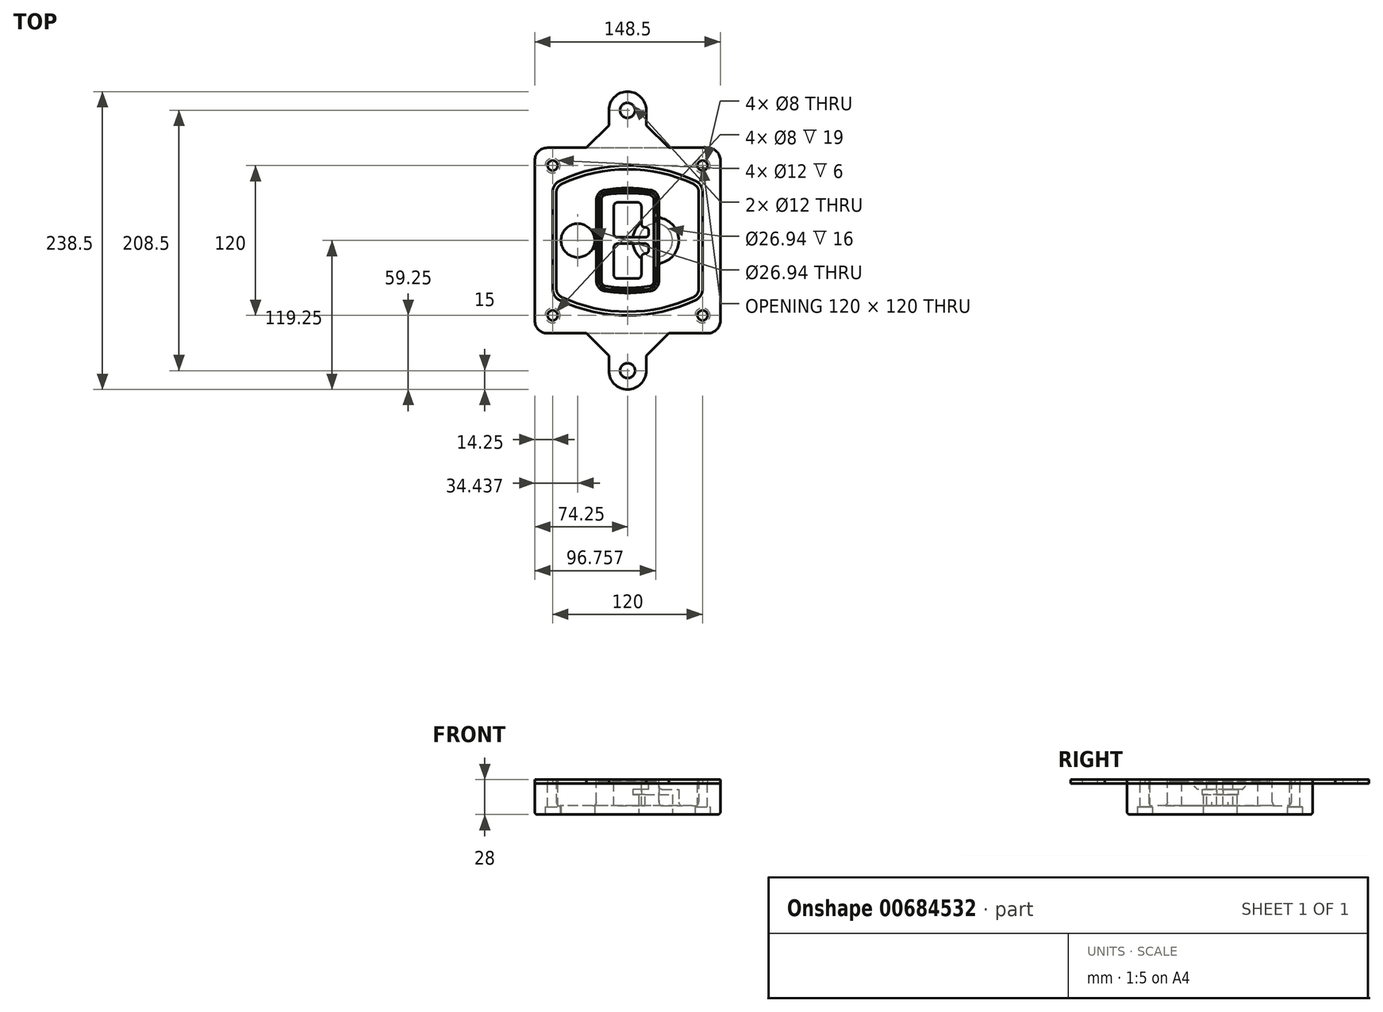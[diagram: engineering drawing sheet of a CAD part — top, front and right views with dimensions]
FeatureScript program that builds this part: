
annotation { "Feature Type Name" : "Feature", "Feature Type Description" : "" }
export const myFeature = defineFeature(function(context is Context, id is Id, definition is map)
    precondition{}
    {
        {
            var Q0;
            Q0=qCreatedBy(makeId("Top.planeOp"),FACE);
            var sketch = newSketch(context, id + "F0", { "sketchPlane" : qUnion([Q0])});
            skPoint(sketch, "E0.rect.middle", {"position": v(0, 0) * mm});
            skLineSegment(sketch, "E1.bottom", {"start": v(-64.25, -74.25) * mm, "end": v(64.25, -74.25) * mm});
            skLineSegment(sketch, "E1.top", {"start": v(-64.25, 74.25) * mm, "end": v(64.25, 74.25) * mm});
            skLineSegment(sketch, "E1.left", {"start": v(-74.25, -64.25) * mm, "end": v(-74.25, 64.25) * mm});
            skLineSegment(sketch, "E1.right", {"start": v(74.25, -64.25) * mm, "end": v(74.25, 64.25) * mm});
            skLineSegment(sketch, "E2", {"start": v(-74.25, 74.25) * mm, "end": v(74.25, -74.25) * mm, "construction": true});
            skLineSegment(sketch, "E3", {"start": v(74.25, 74.25) * mm, "end": v(-74.25, -74.25) * mm, "construction": true});
            skCircle(sketch, "E4", {"center": v(-60, 60) * mm, "radius": 4 * mm});
            skCircle(sketch, "E5", {"center": v(60, 60) * mm, "radius": 4 * mm});
            skCircle(sketch, "E6", {"center": v(60, -60) * mm, "radius": 4 * mm});
            skCircle(sketch, "E7", {"center": v(-60, -60) * mm, "radius": 4 * mm});
            skLineSegment(sketch, "E8", {"start": v(-60, 60) * mm, "end": v(60, 60) * mm, "construction": true});
            skLineSegment(sketch, "E9", {"start": v(60, 60) * mm, "end": v(60, -60) * mm, "construction": true});
            skLineSegment(sketch, "E10", {"start": v(60, -60) * mm, "end": v(-60, -60) * mm, "construction": true});
            skLineSegment(sketch, "E11", {"start": v(-60, -60) * mm, "end": v(-60, 60) * mm, "construction": true});
            skLineSegment(sketch, "E12", {"start": v(-60, 38.83) * mm, "end": v(-60, -38.83) * mm});
            skLineSegment(sketch, "E13", {"start": v(60, 38.83) * mm, "end": v(60, -38.83) * mm});
            skArc(sketch, "E14", {"start": v(54.26, 47.88) * mm, "mid": v(0, 60) * mm, "end": v(-54.26, 47.88) * mm});
            skArc(sketch, "E15", {"start": v(-54.26, -47.88) * mm, "mid": v(0, -60) * mm, "end": v(54.26, -47.88) * mm});
            skLineSegment(sketch, "E16", {"start": v(-60, 0) * mm, "end": v(60, 0) * mm, "construction": true});
            skPoint(sketch, "E17.visualSharp", {"position": v(-60, -45) * mm});
            skArc(sketch, "E17.filletArc", {"start": v(-60, -38.83) * mm, "mid": v(-58.44, -44.2) * mm, "end": v(-54.26, -47.88) * mm});
            skPoint(sketch, "E18.visualSharp", {"position": v(-60, 45) * mm});
            skArc(sketch, "E18.filletArc", {"start": v(-54.26, 47.88) * mm, "mid": v(-58.44, 44.2) * mm, "end": v(-60, 38.83) * mm});
            skPoint(sketch, "E19.visualSharp", {"position": v(60, 45) * mm});
            skArc(sketch, "E19.filletArc", {"start": v(60, 38.83) * mm, "mid": v(58.44, 44.2) * mm, "end": v(54.26, 47.88) * mm});
            skPoint(sketch, "E20.visualSharp", {"position": v(60, -45) * mm});
            skArc(sketch, "E20.filletArc", {"start": v(54.26, -47.88) * mm, "mid": v(58.44, -44.2) * mm, "end": v(60, -38.83) * mm});
            skPoint(sketch, "E21.visualSharp", {"position": v(-74.25, 74.25) * mm});
            skArc(sketch, "E21.filletArc", {"start": v(-64.25, 74.25) * mm, "mid": v(-71.32, 71.32) * mm, "end": v(-74.25, 64.25) * mm});
            skPoint(sketch, "E22.visualSharp", {"position": v(74.25, 74.25) * mm});
            skArc(sketch, "E22.filletArc", {"start": v(74.25, 64.25) * mm, "mid": v(71.32, 71.32) * mm, "end": v(64.25, 74.25) * mm});
            skPoint(sketch, "E23.visualSharp", {"position": v(74.25, -74.25) * mm});
            skArc(sketch, "E23.filletArc", {"start": v(64.25, -74.25) * mm, "mid": v(71.32, -71.32) * mm, "end": v(74.25, -64.25) * mm});
            skPoint(sketch, "E24.visualSharp", {"position": v(-74.25, -74.25) * mm});
            skArc(sketch, "E24.filletArc", {"start": v(-74.25, -64.25) * mm, "mid": v(-71.32, -71.32) * mm, "end": v(-64.25, -74.25) * mm});
            skArc(sketch, "E25.0", {"start": v(57, 38.83) * mm, "mid": v(55.9, 42.58) * mm, "end": v(52.98, 45.17) * mm});
            skLineSegment(sketch, "E25.1", {"start": v(57, 38.83) * mm, "end": v(57, -38.83) * mm});
            skArc(sketch, "E25.2", {"start": v(52.98, -45.17) * mm, "mid": v(55.9, -42.58) * mm, "end": v(57, -38.83) * mm});
            skArc(sketch, "E25.3", {"start": v(-52.98, -45.17) * mm, "mid": v(0, -57) * mm, "end": v(52.98, -45.17) * mm});
            skArc(sketch, "E25.4", {"start": v(-57, -38.83) * mm, "mid": v(-55.9, -42.58) * mm, "end": v(-52.98, -45.17) * mm});
            skArc(sketch, "E25.5", {"start": v(52.98, 45.17) * mm, "mid": v(0, 57) * mm, "end": v(-52.98, 45.17) * mm});
            skLineSegment(sketch, "E25.6", {"start": v(-57, 38.83) * mm, "end": v(-57, -38.83) * mm});
            skArc(sketch, "E25.7", {"start": v(-52.98, 45.17) * mm, "mid": v(-55.9, 42.58) * mm, "end": v(-57, 38.83) * mm});
            skArc(sketch, "E26.0", {"start": v(-55.96, 51.5) * mm, "mid": v(-61.82, 46.33) * mm, "end": v(-64, 38.83) * mm});
            skArc(sketch, "E26.1", {"start": v(55.96, 51.5) * mm, "mid": v(0, 64) * mm, "end": v(-55.96, 51.5) * mm});
            skArc(sketch, "E26.2", {"start": v(64, 38.83) * mm, "mid": v(61.82, 46.33) * mm, "end": v(55.96, 51.5) * mm});
            skLineSegment(sketch, "E26.3", {"start": v(64, 38.83) * mm, "end": v(64, -38.83) * mm});
            skArc(sketch, "E26.4", {"start": v(55.96, -51.5) * mm, "mid": v(61.82, -46.33) * mm, "end": v(64, -38.83) * mm});
            skLineSegment(sketch, "E26.5", {"start": v(-64, 38.83) * mm, "end": v(-64, -38.83) * mm});
            skArc(sketch, "E26.6", {"start": v(-55.96, -51.5) * mm, "mid": v(0, -64) * mm, "end": v(55.96, -51.5) * mm});
            skArc(sketch, "E26.7", {"start": v(-64, -38.83) * mm, "mid": v(-61.82, -46.33) * mm, "end": v(-55.96, -51.5) * mm});
            skLineSegment(sketch, "E27", {"start": v(0, 74.25) * mm, "end": v(0, 104.25) * mm, "construction": true});
            skCircle(sketch, "E28", {"center": v(0, 104.25) * mm, "radius": 6 * mm});
            skArc(sketch, "E29", {"start": v(-15, 104.25) * mm, "mid": v(0, 119.25) * mm, "end": v(15, 104.25) * mm});
            skLineSegment(sketch, "E30", {"start": v(-15, 104.25) * mm, "end": v(-15, 92.25) * mm});
            skLineSegment(sketch, "E31", {"start": v(15, 104.25) * mm, "end": v(15, 92.25) * mm});
            skLineSegment(sketch, "E32", {"start": v(-15, 92.25) * mm, "end": v(-33, 74.25) * mm});
            skLineSegment(sketch, "E33", {"start": v(15, 92.25) * mm, "end": v(33, 74.25) * mm});
            skLineSegment(sketch, "E34", {"start": v(0, -74.25) * mm, "end": v(0, -104.25) * mm, "construction": true});
            skCircle(sketch, "E35", {"center": v(0, -104.25) * mm, "radius": 6 * mm});
            skArc(sketch, "E36", {"start": v(15, -104.25) * mm, "mid": v(0, -119.25) * mm, "end": v(-15, -104.25) * mm});
            skLineSegment(sketch, "E37", {"start": v(15, -104.25) * mm, "end": v(15, -92.25) * mm});
            skLineSegment(sketch, "E38", {"start": v(-15, -104.25) * mm, "end": v(-15, -92.25) * mm});
            skLineSegment(sketch, "E39", {"start": v(15, -92.25) * mm, "end": v(33, -74.25) * mm});
            skLineSegment(sketch, "E40", {"start": v(-15, -92.25) * mm, "end": v(-33, -74.25) * mm});
            skSolve(sketch);
        }
        {
            var Q0;
            Q0=makeQuery(id+"F0.imprint","IMPRINT",FACE,{"disambiguationData":[TD([[makeQuery(id+"F0.imprint","IMPRINT",EDGE,{"derivedFrom":sQuery(id+"F0.wireOp",EDGE,"E1.bottom")}),1.0]])]});
            var Q1;
            Q1=makeQuery(id+"F0.imprint","IMPRINT",FACE,{"disambiguationData":[TD([[makeQuery(id+"F0.imprint","IMPRINT",EDGE,{"derivedFrom":sQuery(id+"F0.wireOp",EDGE,"E12")}),1.0]])]});
            var Q2;
            Q2=makeQuery(id+"F0.imprint","IMPRINT",FACE,{"disambiguationData":[TD([[makeQuery(id+"F0.imprint","IMPRINT",EDGE,{"derivedFrom":sQuery(id+"F0.wireOp",EDGE,"E25.0")}),1.0]])]});
            var Q3;
            Q3=makeQuery(id+"F0.imprint","IMPRINT",FACE,{"disambiguationData":[TD([[makeQuery(id+"F0.imprint","IMPRINT",EDGE,{"derivedFrom":sQuery(id+"F0.wireOp",EDGE,"E12")}),-1.0]])]});
            extrude(context, id + "F1", {"entities" : qUnion([Q0, Q1, Q2, Q3]), "oppositeDirection" : true, "depth" : 25 * mm});
        }
        {
            var Q0;
            Q0=makeQuery(id+"F0.imprint","IMPRINT",FACE,{"disambiguationData":[TD([[makeQuery(id+"F0.imprint","IMPRINT",EDGE,{"derivedFrom":sQuery(id+"F0.wireOp",EDGE,"E12")}),1.0]])]});
            extrude(context, id + "F2", {"entities" : qUnion([Q0]), "operationType" : NewBodyOperationType.ADD, "depth" : 3 * mm});
        }
        {
            var Q0;
            Q0=makeQuery(id+"F0.imprint","IMPRINT",FACE,{"disambiguationData":[TD([[makeQuery(id+"F0.imprint","IMPRINT",EDGE,{"derivedFrom":sQuery(id+"F0.wireOp",EDGE,"E25.0")}),1.0]])]});
            extrude(context, id + "F3", {"entities" : qUnion([Q0]), "operationType" : NewBodyOperationType.REMOVE, "oppositeDirection" : true, "depth" : 18 * mm});
        }
        {
            var Q0;
            Q0=makeQuery(id+"F2.opExtrude","CAP_FACE",FACE,{"disambiguationData":[OSD([sQuery(id+"F0.wireOp",EDGE,"E12"),sQuery(id+"F0.wireOp",EDGE,"E13"),sQuery(id+"F0.wireOp",EDGE,"E14"),sQuery(id+"F0.wireOp",EDGE,"E15"),sQuery(id+"F0.wireOp",EDGE,"E17.filletArc"),sQuery(id+"F0.wireOp",EDGE,"E18.filletArc"),sQuery(id+"F0.wireOp",EDGE,"E19.filletArc"),sQuery(id+"F0.wireOp",EDGE,"E20.filletArc"),sQuery(id+"F0.wireOp",EDGE,"E25.0"),sQuery(id+"F0.wireOp",EDGE,"E25.1"),sQuery(id+"F0.wireOp",EDGE,"E25.2"),sQuery(id+"F0.wireOp",EDGE,"E25.3"),sQuery(id+"F0.wireOp",EDGE,"E25.4"),sQuery(id+"F0.wireOp",EDGE,"E25.5"),sQuery(id+"F0.wireOp",EDGE,"E25.6"),sQuery(id+"F0.wireOp",EDGE,"E25.7")])],"isStart":false});
            var sketch = newSketch(context, id + "F4", { "sketchPlane" : qUnion([Q0])});
            skArc(sketch, "E41.0", {"start": v(-18.34, -40.45) * mm, "mid": v(0, -42) * mm, "end": v(18.34, -40.45) * mm});
            skArc(sketch, "E42.0", {"start": v(18.34, 40.45) * mm, "mid": v(0, 42) * mm, "end": v(-18.34, 40.45) * mm});
            skLineSegment(sketch, "E43", {"start": v(-25, 32.57) * mm, "end": v(-25, -32.57) * mm});
            skLineSegment(sketch, "E44", {"start": v(25, 32.57) * mm, "end": v(25, -32.57) * mm});
            skLineSegment(sketch, "E45", {"start": v(-25, 39.1) * mm, "end": v(25, 39.1) * mm, "construction": true});
            skLineSegment(sketch, "E46", {"start": v(-25, -39.1) * mm, "end": v(25, -39.1) * mm, "construction": true});
            skPoint(sketch, "E47.visualSharp", {"position": v(-25, 39.1) * mm});
            skArc(sketch, "E47.filletArc", {"start": v(-18.34, 40.45) * mm, "mid": v(-23.11, 37.73) * mm, "end": v(-25, 32.57) * mm});
            skPoint(sketch, "E48.visualSharp", {"position": v(25, 39.1) * mm});
            skArc(sketch, "E48.filletArc", {"start": v(25, 32.57) * mm, "mid": v(23.11, 37.73) * mm, "end": v(18.34, 40.45) * mm});
            skPoint(sketch, "E49.visualSharp", {"position": v(25, -39.1) * mm});
            skArc(sketch, "E49.filletArc", {"start": v(18.34, -40.45) * mm, "mid": v(23.11, -37.73) * mm, "end": v(25, -32.57) * mm});
            skPoint(sketch, "E50.visualSharp", {"position": v(-25, -39.1) * mm});
            skArc(sketch, "E50.filletArc", {"start": v(-25, -32.57) * mm, "mid": v(-23.11, -37.73) * mm, "end": v(-18.34, -40.45) * mm});
            skArc(sketch, "E51.0", {"start": v(52.98, 45.17) * mm, "mid": v(0, 57) * mm, "end": v(-52.98, 45.17) * mm});
            skArc(sketch, "E51.1", {"start": v(-52.98, 45.17) * mm, "mid": v(-55.9, 42.58) * mm, "end": v(-57, 38.83) * mm});
            skLineSegment(sketch, "E51.2", {"start": v(-57, 38.83) * mm, "end": v(-57, -38.83) * mm});
            skArc(sketch, "E51.3", {"start": v(-57, -38.83) * mm, "mid": v(-55.9, -42.58) * mm, "end": v(-52.98, -45.17) * mm});
            skArc(sketch, "E51.4", {"start": v(-52.98, -45.17) * mm, "mid": v(0, -57) * mm, "end": v(52.98, -45.17) * mm});
            skArc(sketch, "E51.5", {"start": v(52.98, -45.17) * mm, "mid": v(55.9, -42.58) * mm, "end": v(57, -38.83) * mm});
            skLineSegment(sketch, "E51.6", {"start": v(57, 38.83) * mm, "end": v(57, -38.83) * mm});
            skArc(sketch, "E51.7", {"start": v(57, 38.83) * mm, "mid": v(55.9, 42.58) * mm, "end": v(52.98, 45.17) * mm});
            skLineSegment(sketch, "E52.0", {"start": v(23, 32.57) * mm, "end": v(23, -32.57) * mm});
            skArc(sketch, "E52.1", {"start": v(18, -38.48) * mm, "mid": v(21.58, -36.44) * mm, "end": v(23, -32.57) * mm});
            skArc(sketch, "E52.2", {"start": v(-18, -38.48) * mm, "mid": v(0, -40) * mm, "end": v(18, -38.48) * mm});
            skArc(sketch, "E52.3", {"start": v(-23, -32.57) * mm, "mid": v(-21.58, -36.44) * mm, "end": v(-18, -38.48) * mm});
            skLineSegment(sketch, "E52.4", {"start": v(-23, 32.57) * mm, "end": v(-23, -32.57) * mm});
            skArc(sketch, "E52.5", {"start": v(23, 32.57) * mm, "mid": v(21.58, 36.44) * mm, "end": v(18, 38.48) * mm});
            skArc(sketch, "E52.6", {"start": v(-18, 38.48) * mm, "mid": v(-21.58, 36.44) * mm, "end": v(-23, 32.57) * mm});
            skArc(sketch, "E52.7", {"start": v(18, 38.48) * mm, "mid": v(0, 40) * mm, "end": v(-18, 38.48) * mm});
            skArc(sketch, "E53.0", {"start": v(21, 32.57) * mm, "mid": v(20.06, 35.15) * mm, "end": v(17.67, 36.5) * mm});
            skLineSegment(sketch, "E53.1", {"start": v(21, 32.57) * mm, "end": v(21, -32.57) * mm});
            skArc(sketch, "E53.2", {"start": v(17.67, -36.5) * mm, "mid": v(20.06, -35.15) * mm, "end": v(21, -32.57) * mm});
            skArc(sketch, "E53.3", {"start": v(-17.67, -36.5) * mm, "mid": v(0, -38) * mm, "end": v(17.67, -36.5) * mm});
            skArc(sketch, "E53.4", {"start": v(-21, -32.57) * mm, "mid": v(-20.06, -35.15) * mm, "end": v(-17.67, -36.5) * mm});
            skArc(sketch, "E53.5", {"start": v(17.67, 36.5) * mm, "mid": v(0, 38) * mm, "end": v(-17.67, 36.5) * mm});
            skLineSegment(sketch, "E53.6", {"start": v(-21, 32.57) * mm, "end": v(-21, -32.57) * mm});
            skArc(sketch, "E53.7", {"start": v(-17.67, 36.5) * mm, "mid": v(-20.06, 35.15) * mm, "end": v(-21, 32.57) * mm});
            skLineSegment(sketch, "E54", {"start": v(-25, 0) * mm, "end": v(25, 0) * mm, "construction": true});
            skLineSegment(sketch, "E55", {"start": v(-11, 5.5) * mm, "end": v(-11, 27.5) * mm});
            skLineSegment(sketch, "E56", {"start": v(-8, 30.5) * mm, "end": v(8, 30.5) * mm});
            skLineSegment(sketch, "E57", {"start": v(11, 27.5) * mm, "end": v(11, 13.5) * mm});
            skLineSegment(sketch, "E58", {"start": v(14, 10.5) * mm, "end": v(14, 10.5) * mm});
            skLineSegment(sketch, "E59", {"start": v(17, 7.5) * mm, "end": v(17, 5.5) * mm});
            skLineSegment(sketch, "E60", {"start": v(14, 2.5) * mm, "end": v(-8, 2.5) * mm});
            skPoint(sketch, "E61.visualSharp", {"position": v(-11, 30.5) * mm});
            skArc(sketch, "E61.filletArc", {"start": v(-8, 30.5) * mm, "mid": v(-10.12, 29.62) * mm, "end": v(-11, 27.5) * mm});
            skPoint(sketch, "E62.visualSharp", {"position": v(11, 30.5) * mm});
            skArc(sketch, "E62.filletArc", {"start": v(11, 27.5) * mm, "mid": v(10.12, 29.62) * mm, "end": v(8, 30.5) * mm});
            skPoint(sketch, "E63.visualSharp", {"position": v(11, 10.5) * mm});
            skArc(sketch, "E63.filletArc", {"start": v(11, 13.5) * mm, "mid": v(11.88, 11.38) * mm, "end": v(14, 10.5) * mm});
            skPoint(sketch, "E64.visualSharp", {"position": v(17, 10.5) * mm});
            skArc(sketch, "E64.filletArc", {"start": v(17, 7.5) * mm, "mid": v(16.12, 9.62) * mm, "end": v(14, 10.5) * mm});
            skPoint(sketch, "E65.visualSharp", {"position": v(17, 2.5) * mm});
            skArc(sketch, "E65.filletArc", {"start": v(14, 2.5) * mm, "mid": v(16.12, 3.38) * mm, "end": v(17, 5.5) * mm});
            skPoint(sketch, "E66.visualSharp", {"position": v(-11, 2.5) * mm});
            skArc(sketch, "E66.filletArc", {"start": v(-11, 5.5) * mm, "mid": v(-10.12, 3.38) * mm, "end": v(-8, 2.5) * mm});
            skLineSegment(sketch, "E67.0.MirrorCS", {"start": v(14, -2.5) * mm, "end": v(-8, -2.5) * mm});
            skArc(sketch, "E68.0.MirrorCS", {"start": v(-11, -5.5) * mm, "mid": v(-10.12, -3.38) * mm, "end": v(-8, -2.5) * mm});
            skLineSegment(sketch, "E69.0.MirrorCS", {"start": v(-11, -5.5) * mm, "end": v(-11, -27.5) * mm});
            skArc(sketch, "E70.0.MirrorCS", {"start": v(-8, -30.5) * mm, "mid": v(-10.12, -29.62) * mm, "end": v(-11, -27.5) * mm});
            skLineSegment(sketch, "E71.0.MirrorCS", {"start": v(-8, -30.5) * mm, "end": v(8, -30.5) * mm});
            skArc(sketch, "E72.0.MirrorCS", {"start": v(11, -27.5) * mm, "mid": v(10.12, -29.62) * mm, "end": v(8, -30.5) * mm});
            skLineSegment(sketch, "E73.0.MirrorCS", {"start": v(11, -27.5) * mm, "end": v(11, -13.5) * mm});
            skArc(sketch, "E74.0.MirrorCS", {"start": v(11, -13.5) * mm, "mid": v(11.88, -11.38) * mm, "end": v(14, -10.5) * mm});
            skArc(sketch, "E75.0.MirrorCS", {"start": v(17, -7.5) * mm, "mid": v(16.12, -9.62) * mm, "end": v(14, -10.5) * mm});
            skLineSegment(sketch, "E76.0.MirrorCS", {"start": v(17, -7.5) * mm, "end": v(17, -5.5) * mm});
            skArc(sketch, "E77.0.MirrorCS", {"start": v(14, -2.5) * mm, "mid": v(16.12, -3.38) * mm, "end": v(17, -5.5) * mm});
            skSolve(sketch);
        }
        {
            var Q0;
            Q0=makeQuery(id+"F4.imprint","IMPRINT",FACE,{"disambiguationData":[TD([[makeQuery(id+"F4.imprint","IMPRINT",EDGE,{"derivedFrom":sQuery(id+"F4.wireOp",EDGE,"E41.0")}),1.0]])]});
            var Q1;
            Q1=makeQuery(id+"F4.imprint","IMPRINT",FACE,{"disambiguationData":[TD([[makeQuery(id+"F4.imprint","IMPRINT",EDGE,{"derivedFrom":sQuery(id+"F4.wireOp",EDGE,"E52.0")}),-1.0]])]});
            var Q2;
            Q2=makeQuery(id+"F4.imprint","IMPRINT",FACE,{"disambiguationData":[TD([[makeQuery(id+"F4.imprint","IMPRINT",EDGE,{"derivedFrom":sQuery(id+"F4.wireOp",EDGE,"E53.0")}),1.0]])]});
            extrude(context, id + "F5", {"entities" : qUnion([Q0, Q1, Q2]), "operationType" : NewBodyOperationType.ADD, "endBound" : BoundingType.UP_TO_NEXT, "oppositeDirection" : true, "depth" : 25 * mm});
        }
        {
            var Q0;
            Q0=makeQuery(id+"F4.imprint","IMPRINT",FACE,{"disambiguationData":[TD([[makeQuery(id+"F4.imprint","IMPRINT",EDGE,{"derivedFrom":sQuery(id+"F4.wireOp",EDGE,"E52.0")}),-1.0]])]});
            extrude(context, id + "F6", {"entities" : qUnion([Q0]), "operationType" : NewBodyOperationType.REMOVE, "oppositeDirection" : true, "depth" : 2 * mm});
        }
        {
            var Q0;
            Q0=makeQuery(id+"F1.opExtrude","CAP_FACE",FACE,{"disambiguationData":[OSD([sQuery(id+"F0.wireOp",EDGE,"E1.bottom"),sQuery(id+"F0.wireOp",EDGE,"E1.top"),sQuery(id+"F0.wireOp",EDGE,"E1.left"),sQuery(id+"F0.wireOp",EDGE,"E1.right"),sQuery(id+"F0.wireOp",EDGE,"E4"),sQuery(id+"F0.wireOp",EDGE,"E5"),sQuery(id+"F0.wireOp",EDGE,"E6"),sQuery(id+"F0.wireOp",EDGE,"E7"),sQuery(id+"F0.wireOp",EDGE,"E21.filletArc"),sQuery(id+"F0.wireOp",EDGE,"E22.filletArc"),sQuery(id+"F0.wireOp",EDGE,"E23.filletArc"),sQuery(id+"F0.wireOp",EDGE,"E24.filletArc")])],"isStart":false});
            var sketch = newSketch(context, id + "F7", { "sketchPlane" : qUnion([Q0])});
            skCircle(sketch, "E78", {"center": v(22.5, 0) * mm, "radius": 13.47 * mm});
            skCircle(sketch, "E79", {"center": v(-39.81, 0) * mm, "radius": 13.47 * mm});
            skLineSegment(sketch, "E80", {"start": v(74.25, 0) * mm, "end": v(-74.25, 0) * mm});
            skCircle(sketch, "E81", {"center": v(22.5, 0) * mm, "radius": 18.47 * mm});
            skCircle(sketch, "E82", {"center": v(60, -60) * mm, "radius": 6 * mm});
            skCircle(sketch, "E83", {"center": v(-60, -60) * mm, "radius": 6 * mm});
            skCircle(sketch, "E84", {"center": v(-60, 60) * mm, "radius": 6 * mm});
            skCircle(sketch, "E85", {"center": v(60, 60) * mm, "radius": 6 * mm});
            skSolve(sketch);
        }
        {
            var Q0;
            {var subQ1=sQuery(id+"F7.wireOp",EDGE,"E80");var subQ4=sQuery(id+"F7.wireOp",EDGE,"E78");var subQ6=makeQuery(id+"F7.imprint","INTERSECT",VERTEX,{"disambiguationData":[OD(0.0)],"derivedFrom":[subQ4,subQ1]});Q0=makeQuery(id+"F7.imprint","IMPRINT",FACE,{"disambiguationData":[TD([[makeQuery(id+"F7.imprint","IMPRINT",EDGE,{"disambiguationData":[TD([[subQ6,-1.0]])],"derivedFrom":subQ4}),-1.0]])]});}
            var Q1;
            {var subQ0=sQuery(id+"F7.wireOp",EDGE,"E80");var subQ1=sQuery(id+"F7.wireOp",EDGE,"E78");var subQ3=makeQuery(id+"F7.imprint","INTERSECT",VERTEX,{"disambiguationData":[OD(0.0)],"derivedFrom":[subQ1,subQ0]});Q1=makeQuery(id+"F7.imprint","IMPRINT",FACE,{"disambiguationData":[TD([[makeQuery(id+"F7.imprint","IMPRINT",EDGE,{"disambiguationData":[TD([[subQ3,-1.0]])],"derivedFrom":subQ1}),1.0]])]});}
            var Q2;
            {var subQ0=sQuery(id+"F7.wireOp",EDGE,"E80");var subQ1=sQuery(id+"F7.wireOp",EDGE,"E78");var subQ3=makeQuery(id+"F7.imprint","INTERSECT",VERTEX,{"disambiguationData":[OD(0.0)],"derivedFrom":[subQ1,subQ0]});Q2=makeQuery(id+"F7.imprint","IMPRINT",FACE,{"disambiguationData":[TD([[makeQuery(id+"F7.imprint","IMPRINT",EDGE,{"disambiguationData":[TD([[subQ3,1.0]])],"derivedFrom":subQ1}),1.0]])]});}
            var Q3;
            {var subQ1=sQuery(id+"F7.wireOp",EDGE,"E80");var subQ4=sQuery(id+"F7.wireOp",EDGE,"E78");var subQ6=makeQuery(id+"F7.imprint","INTERSECT",VERTEX,{"disambiguationData":[OD(0.0)],"derivedFrom":[subQ4,subQ1]});Q3=makeQuery(id+"F7.imprint","IMPRINT",FACE,{"disambiguationData":[TD([[makeQuery(id+"F7.imprint","IMPRINT",EDGE,{"disambiguationData":[TD([[subQ6,1.0]])],"derivedFrom":subQ4}),-1.0]])]});}
            extrude(context, id + "F8", {"entities" : qUnion([Q0, Q1, Q2, Q3]), "operationType" : NewBodyOperationType.ADD, "oppositeDirection" : true, "depth" : 20 * mm});
        }
        {
            var Q0;
            {var subQ0=sQuery(id+"F7.wireOp",EDGE,"E80");var subQ1=sQuery(id+"F7.wireOp",EDGE,"E78");var subQ3=makeQuery(id+"F7.imprint","INTERSECT",VERTEX,{"disambiguationData":[OD(0.0)],"derivedFrom":[subQ1,subQ0]});Q0=makeQuery(id+"F7.imprint","IMPRINT",FACE,{"disambiguationData":[TD([[makeQuery(id+"F7.imprint","IMPRINT",EDGE,{"disambiguationData":[TD([[subQ3,-1.0]])],"derivedFrom":subQ1}),1.0]])]});}
            var Q1;
            {var subQ0=sQuery(id+"F7.wireOp",EDGE,"E80");var subQ1=sQuery(id+"F7.wireOp",EDGE,"E78");var subQ3=makeQuery(id+"F7.imprint","INTERSECT",VERTEX,{"disambiguationData":[OD(0.0)],"derivedFrom":[subQ1,subQ0]});Q1=makeQuery(id+"F7.imprint","IMPRINT",FACE,{"disambiguationData":[TD([[makeQuery(id+"F7.imprint","IMPRINT",EDGE,{"disambiguationData":[TD([[subQ3,1.0]])],"derivedFrom":subQ1}),1.0]])]});}
            extrude(context, id + "F9", {"entities" : qUnion([Q0, Q1]), "operationType" : NewBodyOperationType.REMOVE, "oppositeDirection" : true, "depth" : 16 * mm});
        }
        {
            var Q0;
            {var subQ0=sQuery(id+"F7.wireOp",EDGE,"E80");var subQ1=sQuery(id+"F7.wireOp",EDGE,"E79");var subQ3=makeQuery(id+"F7.imprint","INTERSECT",VERTEX,{"disambiguationData":[OD(0.0)],"derivedFrom":[subQ1,subQ0]});Q0=makeQuery(id+"F7.imprint","IMPRINT",FACE,{"disambiguationData":[TD([[makeQuery(id+"F7.imprint","IMPRINT",EDGE,{"disambiguationData":[TD([[subQ3,-1.0]])],"derivedFrom":subQ1}),1.0]])]});}
            var Q1;
            {var subQ0=sQuery(id+"F7.wireOp",EDGE,"E80");var subQ1=sQuery(id+"F7.wireOp",EDGE,"E79");var subQ3=makeQuery(id+"F7.imprint","INTERSECT",VERTEX,{"disambiguationData":[OD(0.0)],"derivedFrom":[subQ1,subQ0]});Q1=makeQuery(id+"F7.imprint","IMPRINT",FACE,{"disambiguationData":[TD([[makeQuery(id+"F7.imprint","IMPRINT",EDGE,{"disambiguationData":[TD([[subQ3,1.0]])],"derivedFrom":subQ1}),1.0]])]});}
            extrude(context, id + "F10", {"entities" : qUnion([Q0, Q1]), "operationType" : NewBodyOperationType.REMOVE, "oppositeDirection" : true, "depth" : 25 * mm});
        }
        {
            var Q0;
            Q0=makeQuery(id+"F7.imprint","IMPRINT",FACE,{"disambiguationData":[TD([[makeQuery(id+"F7.imprint","IMPRINT",EDGE,{"derivedFrom":sQuery(id+"F7.wireOp",EDGE,"E82")}),1.0]])]});
            var Q1;
            Q1=makeQuery(id+"F7.imprint","IMPRINT",FACE,{"disambiguationData":[TD([[makeQuery(id+"F7.imprint","IMPRINT",EDGE,{"derivedFrom":makeQuery(id+"F1.opExtrude","CAP_EDGE",EDGE,{"disambiguationData":[OSD([sQuery(id+"F0.wireOp",EDGE,"E5")])],"isStart":false})}),-1.0]])]});
            var Q2;
            Q2=makeQuery(id+"F7.imprint","IMPRINT",FACE,{"disambiguationData":[TD([[makeQuery(id+"F7.imprint","IMPRINT",EDGE,{"derivedFrom":sQuery(id+"F7.wireOp",EDGE,"E83")}),1.0]])]});
            var Q3;
            Q3=makeQuery(id+"F7.imprint","IMPRINT",FACE,{"disambiguationData":[TD([[makeQuery(id+"F7.imprint","IMPRINT",EDGE,{"derivedFrom":makeQuery(id+"F1.opExtrude","CAP_EDGE",EDGE,{"disambiguationData":[OSD([sQuery(id+"F0.wireOp",EDGE,"E4")])],"isStart":false})}),-1.0]])]});
            var Q4;
            Q4=makeQuery(id+"F7.imprint","IMPRINT",FACE,{"disambiguationData":[TD([[makeQuery(id+"F7.imprint","IMPRINT",EDGE,{"derivedFrom":sQuery(id+"F7.wireOp",EDGE,"E84")}),1.0]])]});
            var Q5;
            Q5=makeQuery(id+"F7.imprint","IMPRINT",FACE,{"disambiguationData":[TD([[makeQuery(id+"F7.imprint","IMPRINT",EDGE,{"derivedFrom":makeQuery(id+"F1.opExtrude","CAP_EDGE",EDGE,{"disambiguationData":[OSD([sQuery(id+"F0.wireOp",EDGE,"E7")])],"isStart":false})}),-1.0]])]});
            var Q6;
            Q6=makeQuery(id+"F7.imprint","IMPRINT",FACE,{"disambiguationData":[TD([[makeQuery(id+"F7.imprint","IMPRINT",EDGE,{"derivedFrom":sQuery(id+"F7.wireOp",EDGE,"E85")}),1.0]])]});
            var Q7;
            Q7=makeQuery(id+"F7.imprint","IMPRINT",FACE,{"disambiguationData":[TD([[makeQuery(id+"F7.imprint","IMPRINT",EDGE,{"derivedFrom":makeQuery(id+"F1.opExtrude","CAP_EDGE",EDGE,{"disambiguationData":[OSD([sQuery(id+"F0.wireOp",EDGE,"E6")])],"isStart":false})}),-1.0]])]});
            extrude(context, id + "F11", {"entities" : qUnion([Q0, Q1, Q2, Q3, Q4, Q5, Q6, Q7]), "operationType" : NewBodyOperationType.REMOVE, "oppositeDirection" : true, "depth" : 6 * mm});
        }
        {
            var Q0;
            Q0=makeQuery(id+"F9.boolean.opBoolean","COPY",FACE,{"derivedFrom":makeQuery(id+"F9.opExtrude","CAP_FACE",FACE,{"disambiguationData":[OSD([sQuery(id+"F7.wireOp",EDGE,"E78")])],"isStart":false})});
            var sketch = newSketch(context, id + "F12", { "sketchPlane" : qUnion([Q0])});
            skArc(sketch, "E86.0", {"start": v(11, 14.45) * mm, "mid": v(6.45, 9.13) * mm, "end": v(4.2, 2.5) * mm});
            skArc(sketch, "E86.1", {"start": v(4.2, -2.5) * mm, "mid": v(6.45, -9.13) * mm, "end": v(11, -14.45) * mm});
            skLineSegment(sketch, "E87", {"start": v(4.2, -2.5) * mm, "end": v(14, -2.5) * mm});
            skLineSegment(sketch, "E88.0", {"start": v(14, 2.5) * mm, "end": v(4.2, 2.5) * mm});
            skArc(sketch, "E88.1", {"start": v(14, 2.5) * mm, "mid": v(16.12, 3.38) * mm, "end": v(17, 5.5) * mm});
            skLineSegment(sketch, "E88.2", {"start": v(17, 7.5) * mm, "end": v(17, 5.5) * mm});
            skArc(sketch, "E88.3", {"start": v(17, 7.5) * mm, "mid": v(16.12, 9.62) * mm, "end": v(14, 10.5) * mm});
            skArc(sketch, "E88.4", {"start": v(11, 13.5) * mm, "mid": v(11.88, 11.38) * mm, "end": v(14, 10.5) * mm});
            skLineSegment(sketch, "E88.5", {"start": v(11, 14.45) * mm, "end": v(11, 13.5) * mm});
            skLineSegment(sketch, "E88.7", {"start": v(14, -2.5) * mm, "end": v(4.2, -2.5) * mm});
            skArc(sketch, "E88.8", {"start": v(14, -2.5) * mm, "mid": v(16.12, -3.38) * mm, "end": v(17, -5.5) * mm});
            skLineSegment(sketch, "E88.9", {"start": v(17, -7.5) * mm, "end": v(17, -5.5) * mm});
            skArc(sketch, "E88.10", {"start": v(17, -7.5) * mm, "mid": v(16.12, -9.62) * mm, "end": v(14, -10.5) * mm});
            skArc(sketch, "E88.11", {"start": v(11, -13.5) * mm, "mid": v(11.88, -11.38) * mm, "end": v(14, -10.5) * mm});
            skLineSegment(sketch, "E88.12", {"start": v(11, -14.45) * mm, "end": v(11, -13.5) * mm});
            skPoint(sketch, "E89.orphan", {"position": v(11, -27.5) * mm});
            skPoint(sketch, "E90.orphan", {"position": v(-8, -2.5) * mm});
            skPoint(sketch, "E91.orphan", {"position": v(-8, 2.5) * mm});
            skPoint(sketch, "E92.orphan", {"position": v(11, 27.5) * mm});
            skSolve(sketch);
        }
        {
            var Q0;
            {var subQ7=sQuery(id+"F12.wireOp",EDGE,"E86.0");var subQ14=sQuery(id+"F12.wireOp",EDGE,"E86.1");var subQ16=sQuery(id+"F12.wireOp",EDGE,"E88.1");var subQ18=sQuery(id+"F12.wireOp",EDGE,"E88.8");Q0=qUnion([makeQuery(id+"F12.imprint","IMPRINT",FACE,{"disambiguationData":[TD([[makeQuery(id+"F12.imprint","IMPRINT",EDGE,{"derivedFrom":subQ7}),1.0]])]}),makeQuery(id+"F12.imprint","IMPRINT",FACE,{"disambiguationData":[TD([[makeQuery(id+"F12.imprint","IMPRINT",EDGE,{"derivedFrom":subQ14}),1.0]])]}),makeQuery(id+"F12.imprint","IMPRINT",FACE,{"disambiguationData":[TD([[makeQuery(id+"F12.imprint","IMPRINT",EDGE,{"derivedFrom":subQ16}),1.0]])]}),makeQuery(id+"F12.imprint","IMPRINT",FACE,{"disambiguationData":[TD([[makeQuery(id+"F12.imprint","IMPRINT",EDGE,{"derivedFrom":subQ18}),-1.0]])]})]);}
            var Q1;
            Q1=makeQuery(id+"F5.boolean.opBoolean","SPLIT",FACE,{"disambiguationData":[TD([makeQuery(id+"F5.opExtrude","SWEPT_FACE",FACE,{"disambiguationData":[OSD([sQuery(id+"F4.wireOp",EDGE,"E55")])]})])],"derivedFrom":makeQuery(id+"F3.boolean.opBoolean","COPY",FACE,{"derivedFrom":makeQuery(id+"F3.opExtrude","CAP_FACE",FACE,{"disambiguationData":[OSD([sQuery(id+"F0.wireOp",EDGE,"E25.0"),sQuery(id+"F0.wireOp",EDGE,"E25.1"),sQuery(id+"F0.wireOp",EDGE,"E25.2"),sQuery(id+"F0.wireOp",EDGE,"E25.3"),sQuery(id+"F0.wireOp",EDGE,"E25.4"),sQuery(id+"F0.wireOp",EDGE,"E25.5"),sQuery(id+"F0.wireOp",EDGE,"E25.6"),sQuery(id+"F0.wireOp",EDGE,"E25.7")])],"isStart":false})})});
            extrude(context, id + "F13", {"entities" : qUnion([Q0]), "operationType" : NewBodyOperationType.REMOVE, "endBound" : BoundingType.UP_TO_SURFACE, "endBoundEntityFace" : qUnion([Q1]), "depth" : 25 * mm});
        }
        {
            var Q0;
            Q0=makeQuery(id+"F3.boolean.opBoolean","COPY",EDGE,{"derivedFrom":makeQuery(id+"F3.opExtrude","CAP_EDGE",EDGE,{"disambiguationData":[OSD([sQuery(id+"F0.wireOp",EDGE,"E25.6")])],"isStart":false})});
            var Q1;
            Q1=makeQuery(id+"F8.boolean.opBoolean","INTERSECT",EDGE,{"derivedFrom":[makeQuery(id+"F5.opExtrude","SWEPT_FACE",FACE,{"disambiguationData":[OSD([sQuery(id+"F4.wireOp",EDGE,"E44")])]}),makeQuery(id+"F8.opExtrude","CAP_FACE",FACE,{"disambiguationData":[OSD([sQuery(id+"F7.wireOp",EDGE,"E81")])],"isStart":false})]});
            var Q2;
            Q2=makeQuery(id+"F8.boolean.opBoolean","INTERSECT",EDGE,{"disambiguationData":[OD(1.0)],"derivedFrom":[makeQuery(id+"F5.opExtrude","SWEPT_FACE",FACE,{"disambiguationData":[OSD([sQuery(id+"F4.wireOp",EDGE,"E44")])]}),makeQuery(id+"F8.opExtrude","SWEPT_FACE",FACE,{"disambiguationData":[OSD([sQuery(id+"F7.wireOp",EDGE,"E81")])]})]});
            var Q3;
            {var subQ0=sQuery(id+"F4.wireOp",EDGE,"E44");Q3=makeQuery(id+"F8.boolean.opBoolean","SPLIT",EDGE,{"disambiguationData":[TD([makeQuery(id+"F5.opExtrude","SWEPT_FACE",FACE,{"disambiguationData":[OSD([sQuery(id+"F4.wireOp",EDGE,"E49.filletArc")])]})])],"derivedFrom":makeQuery(id+"F5.opExtrude","CAP_EDGE",EDGE,{"disambiguationData":[OSD([subQ0])],"isStart":false})});}
            var Q4;
            {var subQ0=sQuery(id+"F0.wireOp",EDGE,"E25.7");var subQ1=sQuery(id+"F0.wireOp",EDGE,"E25.1");var subQ2=sQuery(id+"F0.wireOp",EDGE,"E25.6");var subQ3=sQuery(id+"F0.wireOp",EDGE,"E25.5");var subQ4=sQuery(id+"F0.wireOp",EDGE,"E25.4");var subQ5=sQuery(id+"F0.wireOp",EDGE,"E25.0");var subQ6=sQuery(id+"F0.wireOp",EDGE,"E25.2");var subQ7=sQuery(id+"F0.wireOp",EDGE,"E25.3");Q4=makeQuery(id+"F8.boolean.opBoolean","INTERSECT",EDGE,{"derivedFrom":[makeQuery(id+"F5.boolean.opBoolean","SPLIT",FACE,{"disambiguationData":[TD([makeQuery(id+"F2.opExtrude","SWEPT_FACE",FACE,{"disambiguationData":[OSD([subQ5])]})])],"derivedFrom":makeQuery(id+"F3.boolean.opBoolean","COPY",FACE,{"derivedFrom":makeQuery(id+"F3.opExtrude","CAP_FACE",FACE,{"disambiguationData":[OSD([subQ5,subQ1,subQ6,subQ7,subQ4,subQ3,subQ2,subQ0])],"isStart":false})})}),makeQuery(id+"F8.opExtrude","SWEPT_FACE",FACE,{"disambiguationData":[OSD([sQuery(id+"F7.wireOp",EDGE,"E81")])]})]});}
            var Q5;
            Q5=makeQuery(id+"F8.boolean.opBoolean","INTERSECT",EDGE,{"disambiguationData":[OD(0.0)],"derivedFrom":[makeQuery(id+"F5.opExtrude","SWEPT_FACE",FACE,{"disambiguationData":[OSD([sQuery(id+"F4.wireOp",EDGE,"E44")])]}),makeQuery(id+"F8.opExtrude","SWEPT_FACE",FACE,{"disambiguationData":[OSD([sQuery(id+"F7.wireOp",EDGE,"E81")])]})]});
            fillet(context, id + "F14", {"entities" : qUnion([Q0, Q1, Q2, Q3, Q4, Q5]), "radius" : 3 * mm, "tangentPropagation" : true, "allowEdgeOverflow" : false});
        }
        {
            var Q0;
            Q0=makeQuery(id+"F1.opExtrude","CAP_EDGE",EDGE,{"disambiguationData":[OSD([sQuery(id+"F0.wireOp",EDGE,"E1.bottom")])],"isStart":false});
            fillet(context, id + "F15", {"entities" : qUnion([Q0]), "radius" : 2 * mm, "tangentPropagation" : true, "allowEdgeOverflow" : false});
        }
        {
            var Q0;
            Q0=qSketchRegion(id+"F0",true);
            var Q1;
            Q1=makeQuery(id+"F0.imprint","IMPRINT",FACE,{"disambiguationData":[TD([[makeQuery(id+"F0.imprint","IMPRINT",EDGE,{"derivedFrom":sQuery(id+"F0.wireOp",EDGE,"E12")}),-1.0]])]});
            var Q2;
            {var subQ0=sQuery(id+"F4.wireOp",EDGE,"E50.filletArc");var subQ1=sQuery(id+"F4.wireOp",EDGE,"E49.filletArc");var subQ2=sQuery(id+"F4.wireOp",EDGE,"E48.filletArc");var subQ3=sQuery(id+"F4.wireOp",EDGE,"E47.filletArc");var subQ4=sQuery(id+"F4.wireOp",EDGE,"E41.0");var subQ5=sQuery(id+"F4.wireOp",EDGE,"E44");var subQ6=sQuery(id+"F4.wireOp",EDGE,"E42.0");var subQ7=sQuery(id+"F4.wireOp",EDGE,"E43");Q2=makeQuery(id+"F6.boolean.opBoolean","SPLIT",FACE,{"disambiguationData":[TD([makeQuery(id+"F5.opExtrude","SWEPT_FACE",FACE,{"disambiguationData":[OSD([subQ4])]})])],"derivedFrom":makeQuery(id+"F5.opExtrude","CAP_FACE",FACE,{"disambiguationData":[OSD([subQ4,subQ6,subQ7,subQ5,subQ3,subQ2,subQ1,subQ0,sQuery(id+"F4.wireOp",EDGE,"E55"),sQuery(id+"F4.wireOp",EDGE,"E56"),sQuery(id+"F4.wireOp",EDGE,"E57"),sQuery(id+"F4.wireOp",EDGE,"E59"),sQuery(id+"F4.wireOp",EDGE,"E60"),sQuery(id+"F4.wireOp",EDGE,"E61.filletArc"),sQuery(id+"F4.wireOp",EDGE,"E62.filletArc"),sQuery(id+"F4.wireOp",EDGE,"E63.filletArc"),sQuery(id+"F4.wireOp",EDGE,"E64.filletArc"),sQuery(id+"F4.wireOp",EDGE,"E65.filletArc"),sQuery(id+"F4.wireOp",EDGE,"E66.filletArc"),sQuery(id+"F4.wireOp",EDGE,"E67.0.MirrorCS"),sQuery(id+"F4.wireOp",EDGE,"E68.0.MirrorCS"),sQuery(id+"F4.wireOp",EDGE,"E69.0.MirrorCS"),sQuery(id+"F4.wireOp",EDGE,"E70.0.MirrorCS"),sQuery(id+"F4.wireOp",EDGE,"E71.0.MirrorCS"),sQuery(id+"F4.wireOp",EDGE,"E72.0.MirrorCS"),sQuery(id+"F4.wireOp",EDGE,"E73.0.MirrorCS"),sQuery(id+"F4.wireOp",EDGE,"E74.0.MirrorCS"),sQuery(id+"F4.wireOp",EDGE,"E75.0.MirrorCS"),sQuery(id+"F4.wireOp",EDGE,"E76.0.MirrorCS"),sQuery(id+"F4.wireOp",EDGE,"E77.0.MirrorCS")])],"isStart":true})});}
            extrude(context, id + "F16", {"entities" : qUnion([Q0, Q1]), "endBound" : BoundingType.UP_TO_SURFACE, "depth" : 25 * mm, "endBoundEntityFace" : qUnion([Q2]), "offsetDistance" : 25 * mm});
        }
    });
